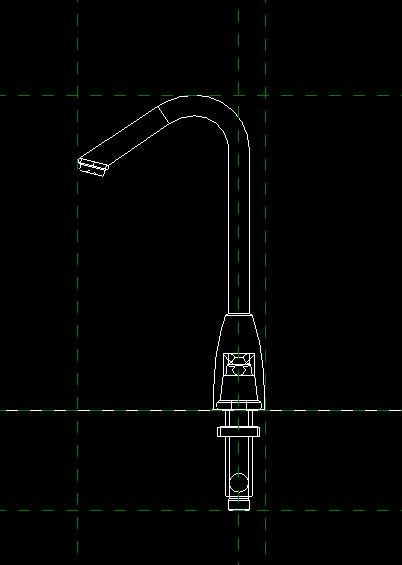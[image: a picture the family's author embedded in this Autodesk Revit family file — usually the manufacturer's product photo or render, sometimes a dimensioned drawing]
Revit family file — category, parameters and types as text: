
# Revit family: AV5070001_Grifería Lavaplatos 8 pulgadas Aluvia Palanca
name_source: partatom
category: Plumbing Fixtures
units: mm (PartAtom-declared; Revit-internal decimal feet)

## family parameters
Cut with Voids When Loaded = No
Host = Face
OmniClass Number = 23.45.55.14
OmniClass Title = Single Faucets
Part Type = Normal
Room Calculation Point = No
Round Connector Dimension = Use Diameter
Shared = No

## types (1)
- AV5070001_Grifería Lavaplatos 8 pulgadas Aluvia Palanca
    Alto = 336 mm  [stored 1.10236 ft]
    Ancho = 320 mm  [stored 1.04987 ft]
    Default Elevation = 1219 mm
    Fabricante = Corona
    Garantía = 30 años
    Peso neto = 445 gr. - 0,98 lb
    Presion maxima = 125 psi (862 Kpa)
    Presion minima = 20 psi (138 Kpa)
    Profundidad = 200 mm  [stored 0.656168 ft]
    Referencia = AV5070001
    Temperatura de uso = 5ºC a 71ºC
    URL = https://corona.co

note: [stored X ft] marks values corroborated as IEEE doubles in the binary element streams (Revit-internal decimal feet)

## geometry (parser evidence)
native form markers: Sweep x5
no freeform markers — native parametric forms only
